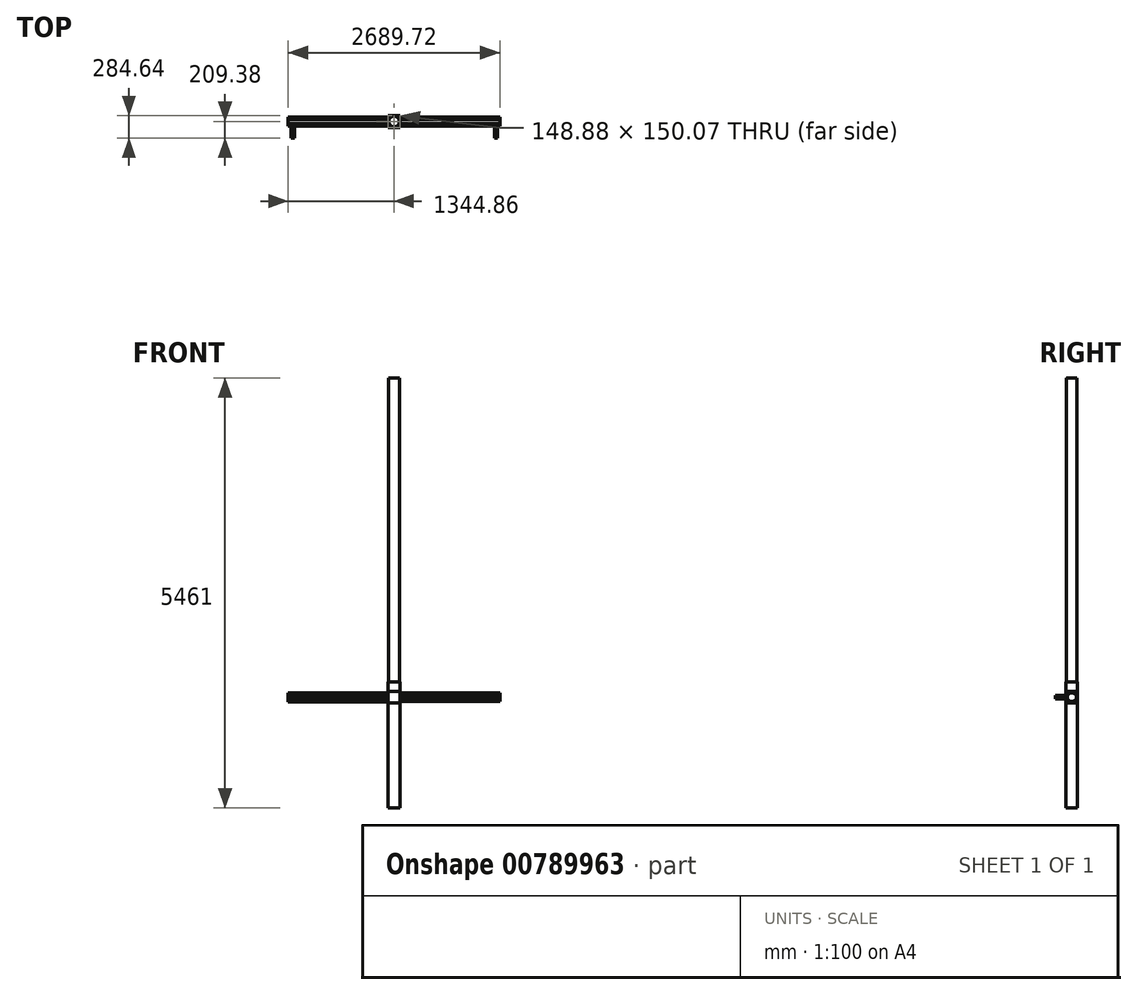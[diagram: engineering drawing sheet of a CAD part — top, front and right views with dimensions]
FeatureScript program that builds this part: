
annotation { "Feature Type Name" : "Feature", "Feature Type Description" : "" }
export const myFeature = defineFeature(function(context is Context, id is Id, definition is map)
    precondition{}
    {
        {
            var Q0;
            Q0=qCreatedBy(makeId("Top.planeOp"),FACE);
            var sketch = newSketch(context, id + "F0", { "sketchPlane" : qUnion([Q0])});
            skCircle(sketch, "E0", {"center": v(0, 0) * mm, "radius": 67.14 * mm});
            skSolve(sketch);
        }
        {
            var Q0;
            Q0 = qSketchRegion(id + "F0", true);
            extrude(context, id + "F1", {"entities" : qUnion([Q0]), "depth" : 4495.8 * mm, "offsetDistance" : 25.4 * mm});
        }
        {
            var Q0;
            Q0=qCreatedBy(makeId("Top.planeOp"),FACE);
            var sketch = newSketch(context, id + "F2", { "sketchPlane" : qUnion([Q0])});
            skLineSegment(sketch, "E1.bottom", {"start": v(74.44, 75.03) * mm, "end": v(-74.44, 75.03) * mm});
            skLineSegment(sketch, "E1.top", {"start": v(74.44, -75.03) * mm, "end": v(-74.44, -75.03) * mm});
            skLineSegment(sketch, "E1.left", {"start": v(74.44, 75.03) * mm, "end": v(74.44, -75.03) * mm});
            skLineSegment(sketch, "E1.right", {"start": v(-74.44, 75.03) * mm, "end": v(-74.44, -75.03) * mm});
            skPoint(sketch, "E1.middle", {"position": v(0, 0) * mm});
            skSolve(sketch);
        }
        {
            var Q0;
            Q0 = qSketchRegion(id + "F2", true);
            extrude(context, id + "F3", {"entities" : qUnion([Q0]), "operationType" : NewBodyOperationType.ADD, "depth" : 635 * mm, "offsetDistance" : 25.4 * mm});
        }
        {
            var Q0;
            Q0=qCreatedBy(makeId("Top.planeOp"),FACE);
            cPlane(context, id + "F4", {"entities" : qUnion([Q0]), "cplaneType" : CPlaneType.OFFSET, "offset" : 370.84 * mm, "width" : 152.4 * mm, "height" : 152.4 * mm});
        }
        {
            var Q0;
            Q0=qCreatedBy(id+"F4.planeOp",FACE);
            var sketch = newSketch(context, id + "F5", { "sketchPlane" : qUnion([Q0])});
            skLineSegment(sketch, "E2.bottom", {"start": v(74.86, 75.26) * mm, "end": v(-74.86, 75.26) * mm});
            skLineSegment(sketch, "E2.top", {"start": v(74.86, -75.26) * mm, "end": v(-74.86, -75.26) * mm});
            skLineSegment(sketch, "E2.left", {"start": v(74.86, 75.26) * mm, "end": v(74.86, -75.26) * mm});
            skLineSegment(sketch, "E2.right", {"start": v(-74.86, 75.26) * mm, "end": v(-74.86, -75.26) * mm});
            skPoint(sketch, "E2.middle", {"position": v(0, 0) * mm});
            skSolve(sketch);
        }
        {
            var Q0;
            Q0 = qSketchRegion(id + "F5", true);
            extrude(context, id + "F6", {"entities" : qUnion([Q0]), "operationType" : NewBodyOperationType.ADD, "depth" : 142.24 * mm, "offsetDistance" : 25.4 * mm});
        }
        {
            var Q0;
            Q0=makeQuery(id+"F6.opExtrude","SWEPT_FACE",FACE,{"disambiguationData":[OSD([sQuery(id+"F5.wireOp",EDGE,"E2.left")])]});
            var sketch = newSketch(context, id + "F7", { "sketchPlane" : qUnion([Q0])});
            skLineSegment(sketch, "E3", {"start": v(-75.26, 513.08) * mm, "end": v(75.26, 370.84) * mm, "construction": true});
            skLineSegment(sketch, "E4", {"start": v(-75.26, 370.84) * mm, "end": v(75.26, 513.08) * mm, "construction": true});
            skCircle(sketch, "E5.cCircle", {"center": v(0, 441.96) * mm, "radius": 56.98 * mm, "construction": true});
            skLineSegment(sketch, "E5.0", {"start": v(-23.6, 498.94) * mm, "end": v(23.6, 498.94) * mm});
            skLineSegment(sketch, "E5.1", {"start": v(23.6, 498.94) * mm, "end": v(56.98, 465.56) * mm});
            skLineSegment(sketch, "E5.2", {"start": v(56.98, 465.56) * mm, "end": v(56.98, 418.36) * mm});
            skLineSegment(sketch, "E5.3", {"start": v(56.98, 418.36) * mm, "end": v(23.6, 384.98) * mm});
            skLineSegment(sketch, "E5.4", {"start": v(23.6, 384.98) * mm, "end": v(-23.6, 384.98) * mm});
            skLineSegment(sketch, "E5.5", {"start": v(-23.6, 384.98) * mm, "end": v(-56.98, 418.36) * mm});
            skLineSegment(sketch, "E5.6", {"start": v(-56.98, 418.36) * mm, "end": v(-56.98, 465.56) * mm});
            skLineSegment(sketch, "E5.7", {"start": v(-56.98, 465.56) * mm, "end": v(-23.6, 498.94) * mm});
            skPoint(sketch, "E5.0.midPoint", {"position": v(0, 498.94) * mm});
            skSolve(sketch);
        }
        {
            var Q0;
            Q0 = qSketchRegion(id + "F7", true);
            extrude(context, id + "F8", {"entities" : qUnion([Q0]), "operationType" : NewBodyOperationType.ADD, "depth" : 1270 * mm, "offsetDistance" : 25.4 * mm});
        }
        {
            var Q0;
            Q0=makeQuery(id+"F6.opExtrude","SWEPT_FACE",FACE,{"disambiguationData":[OSD([sQuery(id+"F5.wireOp",EDGE,"E2.right")])]});
            var sketch = newSketch(context, id + "F9", { "sketchPlane" : qUnion([Q0])});
            skLineSegment(sketch, "E6", {"start": v(-75.26, 508.33) * mm, "end": v(75.26, 366.1) * mm, "construction": true});
            skLineSegment(sketch, "E7", {"start": v(-75.26, 366.1) * mm, "end": v(75.26, 508.33) * mm, "construction": true});
            skCircle(sketch, "E8.cCircle", {"center": v(0, 437.21) * mm, "radius": 56.98 * mm, "construction": true});
            skLineSegment(sketch, "E8.0", {"start": v(-23.6, 494.2) * mm, "end": v(23.6, 494.2) * mm});
            skLineSegment(sketch, "E8.1", {"start": v(23.6, 494.2) * mm, "end": v(56.98, 460.81) * mm});
            skLineSegment(sketch, "E8.2", {"start": v(56.98, 460.81) * mm, "end": v(56.98, 413.6) * mm});
            skLineSegment(sketch, "E8.3", {"start": v(56.98, 413.6) * mm, "end": v(23.6, 380.23) * mm});
            skLineSegment(sketch, "E8.4", {"start": v(23.6, 380.23) * mm, "end": v(-23.6, 380.23) * mm});
            skLineSegment(sketch, "E8.5", {"start": v(-23.6, 380.23) * mm, "end": v(-56.98, 413.6) * mm});
            skLineSegment(sketch, "E8.6", {"start": v(-56.98, 413.6) * mm, "end": v(-56.98, 460.81) * mm});
            skLineSegment(sketch, "E8.7", {"start": v(-56.98, 460.81) * mm, "end": v(-23.6, 494.2) * mm});
            skPoint(sketch, "E8.0.midPoint", {"position": v(0, 494.2) * mm});
            skSolve(sketch);
        }
        {
            var Q0;
            Q0=makeQuery(id+"F9.imprint","IMPRINT",FACE,{"disambiguationData":[TD([[makeQuery(id+"F9.imprint","IMPRINT",EDGE,{"derivedFrom":sQuery(id+"F9.wireOp",EDGE,"E8.0")}),-1.0]])]});
            extrude(context, id + "F10", {"entities" : qUnion([Q0]), "operationType" : NewBodyOperationType.ADD, "depth" : 1270 * mm, "offsetDistance" : 25.4 * mm});
        }
        {
            var Q0;
            Q0=makeQuery(id+"F10.opExtrude","SWEPT_FACE",FACE,{"disambiguationData":[OSD([sQuery(id+"F9.wireOp",EDGE,"E8.2")])]});
            var sketch = newSketch(context, id + "F11", { "sketchPlane" : qUnion([Q0])});
            skLineSegment(sketch, "E9", {"start": v(-1344.86, 437.21) * mm, "end": v(-1286.17, 437.21) * mm, "construction": true});
            skCircle(sketch, "E10.cCircle", {"center": v(-1286.17, 437.21) * mm, "radius": 20.32 * mm, "construction": true});
            skLineSegment(sketch, "E10.0", {"start": v(-1294.62, 457.52) * mm, "end": v(-1277.79, 457.54) * mm});
            skLineSegment(sketch, "E10.1", {"start": v(-1277.79, 457.54) * mm, "end": v(-1265.86, 445.66) * mm});
            skLineSegment(sketch, "E10.2", {"start": v(-1265.86, 445.66) * mm, "end": v(-1265.84, 428.83) * mm});
            skLineSegment(sketch, "E10.3", {"start": v(-1265.84, 428.83) * mm, "end": v(-1277.72, 416.9) * mm});
            skLineSegment(sketch, "E10.4", {"start": v(-1277.72, 416.9) * mm, "end": v(-1294.56, 416.88) * mm});
            skLineSegment(sketch, "E10.5", {"start": v(-1294.56, 416.88) * mm, "end": v(-1306.48, 428.76) * mm});
            skLineSegment(sketch, "E10.6", {"start": v(-1306.48, 428.76) * mm, "end": v(-1306.5, 445.6) * mm});
            skLineSegment(sketch, "E10.7", {"start": v(-1306.5, 445.6) * mm, "end": v(-1294.62, 457.52) * mm});
            skPoint(sketch, "E10.0.midPoint", {"position": v(-1286.2, 457.53) * mm});
            skSolve(sketch);
        }
        {
            var Q0;
            Q0=makeQuery(id+"F8.opExtrude","SWEPT_FACE",FACE,{"disambiguationData":[OSD([sQuery(id+"F7.wireOp",EDGE,"E5.6")])]});
            var sketch = newSketch(context, id + "F12", { "sketchPlane" : qUnion([Q0])});
            skLineSegment(sketch, "E11", {"start": v(1344.86, 441.96) * mm, "end": v(1294.06, 441.96) * mm, "construction": true});
            skCircle(sketch, "E12.cCircle", {"center": v(1294.06, 441.96) * mm, "radius": 20.32 * mm, "construction": true});
            skLineSegment(sketch, "E12.0", {"start": v(1314.38, 450.38) * mm, "end": v(1314.38, 433.54) * mm});
            skLineSegment(sketch, "E12.1", {"start": v(1314.38, 433.54) * mm, "end": v(1302.47, 421.64) * mm});
            skLineSegment(sketch, "E12.2", {"start": v(1302.47, 421.64) * mm, "end": v(1285.64, 421.64) * mm});
            skLineSegment(sketch, "E12.3", {"start": v(1285.64, 421.64) * mm, "end": v(1273.74, 433.54) * mm});
            skLineSegment(sketch, "E12.4", {"start": v(1273.74, 433.54) * mm, "end": v(1273.74, 450.38) * mm});
            skLineSegment(sketch, "E12.5", {"start": v(1273.74, 450.38) * mm, "end": v(1285.64, 462.28) * mm});
            skLineSegment(sketch, "E12.6", {"start": v(1285.64, 462.28) * mm, "end": v(1302.47, 462.28) * mm});
            skLineSegment(sketch, "E12.7", {"start": v(1302.47, 462.28) * mm, "end": v(1314.38, 450.38) * mm});
            skPoint(sketch, "E12.0.midPoint", {"position": v(1314.38, 441.96) * mm});
            skSolve(sketch);
        }
        {
            var Q0;
            Q0=makeQuery(id+"F11.imprint","IMPRINT",FACE,{"disambiguationData":[TD([[makeQuery(id+"F11.imprint","IMPRINT",EDGE,{"derivedFrom":sQuery(id+"F11.wireOp",EDGE,"E10.0")}),-1.0]])]});
            var Q1;
            Q1=makeQuery(id+"F12.imprint","IMPRINT",FACE,{"disambiguationData":[TD([[makeQuery(id+"F12.imprint","IMPRINT",EDGE,{"derivedFrom":sQuery(id+"F12.wireOp",EDGE,"E12.0")}),-1.0]])]});
            extrude(context, id + "F13", {"entities" : qUnion([Q0, Q1]), "operationType" : NewBodyOperationType.ADD, "depth" : 152.4 * mm, "offsetDistance" : 25.4 * mm});
        }
        {
            var Q0;
            Q0=makeQuery(id+"F3.boolean.opBoolean","MERGE",FACE,{"derivedFrom":[makeQuery(id+"F1.opExtrude","CAP_FACE",FACE,{"disambiguationData":[OSD([sQuery(id+"F0.wireOp",EDGE,"E0")])],"isStart":true}),makeQuery(id+"F3.opExtrude","CAP_FACE",FACE,{"disambiguationData":[OSD([sQuery(id+"F2.wireOp",EDGE,"E1.bottom"),sQuery(id+"F2.wireOp",EDGE,"E1.top"),sQuery(id+"F2.wireOp",EDGE,"E1.left"),sQuery(id+"F2.wireOp",EDGE,"E1.right")])],"isStart":true})]});
            extrude(context, id + "F14", {"entities" : qUnion([Q0]), "operationType" : NewBodyOperationType.ADD, "depth" : 965.2 * mm, "offsetDistance" : 25.4 * mm});
        }
    });
